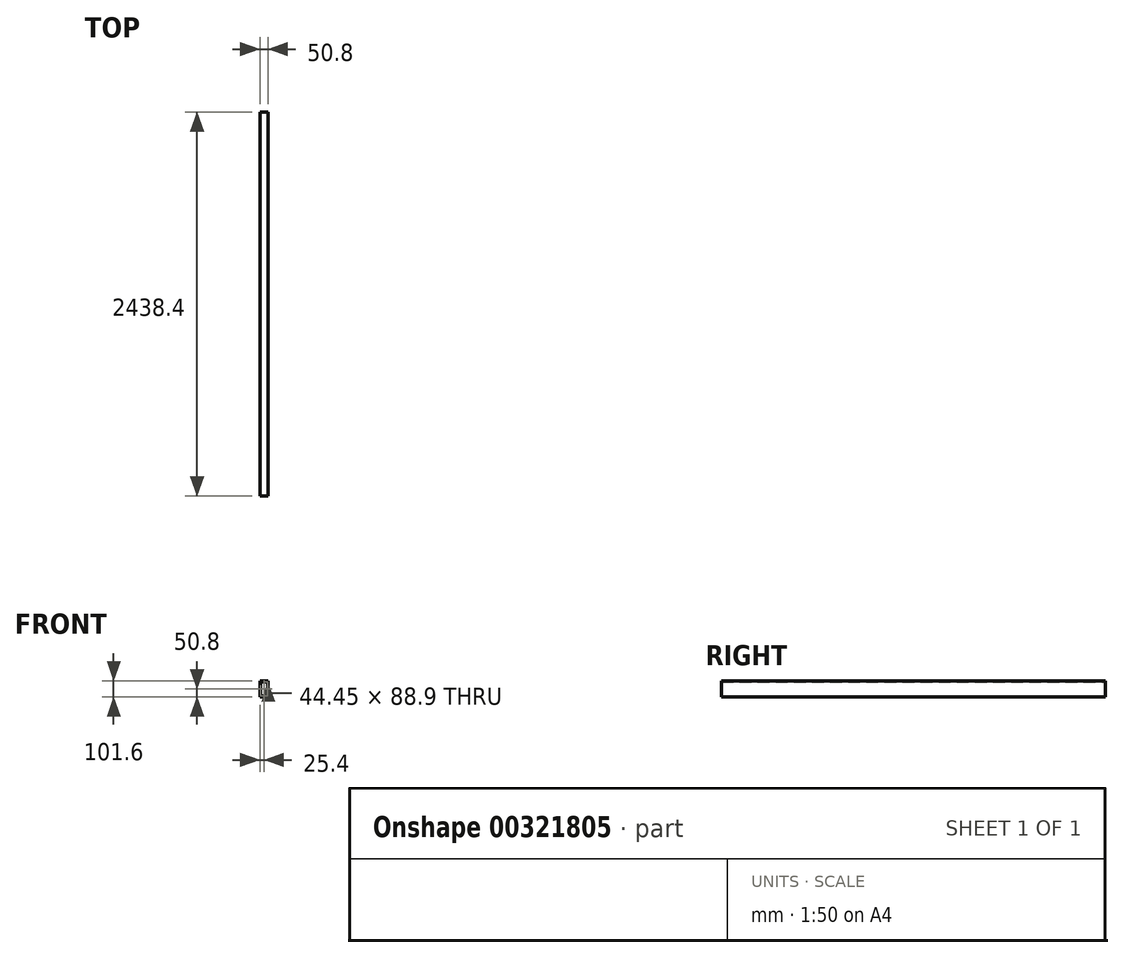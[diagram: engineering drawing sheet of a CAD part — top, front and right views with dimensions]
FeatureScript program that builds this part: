
annotation { "Feature Type Name" : "Feature", "Feature Type Description" : "" }
export const myFeature = defineFeature(function(context is Context, id is Id, definition is map)
    precondition{}
    {
        {
            var Q0;
            Q0=qCreatedBy(makeId("Front.planeOp"),FACE);
            var sketch = newSketch(context, id + "F0", { "sketchPlane" : qUnion([Q0])});
            skLineSegment(sketch, "E0.bottom", {"start": v(-22.23, 44.45) * mm, "end": v(22.23, 44.45) * mm});
            skLineSegment(sketch, "E0.top", {"start": v(-22.23, -44.45) * mm, "end": v(22.23, -44.45) * mm});
            skLineSegment(sketch, "E0.left", {"start": v(-22.23, 44.45) * mm, "end": v(-22.23, -44.45) * mm});
            skLineSegment(sketch, "E0.right", {"start": v(22.23, 44.45) * mm, "end": v(22.23, -44.45) * mm});
            skPoint(sketch, "E0.middle", {"position": v(0, 0) * mm});
            skLineSegment(sketch, "E1.bottom", {"start": v(-25.4, 50.8) * mm, "end": v(25.4, 50.8) * mm});
            skLineSegment(sketch, "E1.top", {"start": v(-25.4, -50.8) * mm, "end": v(25.4, -50.8) * mm});
            skLineSegment(sketch, "E1.left", {"start": v(-25.4, 50.8) * mm, "end": v(-25.4, -50.8) * mm});
            skLineSegment(sketch, "E1.right", {"start": v(25.4, 50.8) * mm, "end": v(25.4, -50.8) * mm});
            skSolve(sketch);
        }
        {
            var Q0;
            Q0 = qSketchRegion(id + "F0", true);
            extrude(context, id + "F1", {"entities" : qUnion([Q0]), "endBound" : BoundingType.SYMMETRIC, "depth" : 2438.4 * mm});
        }
    });
